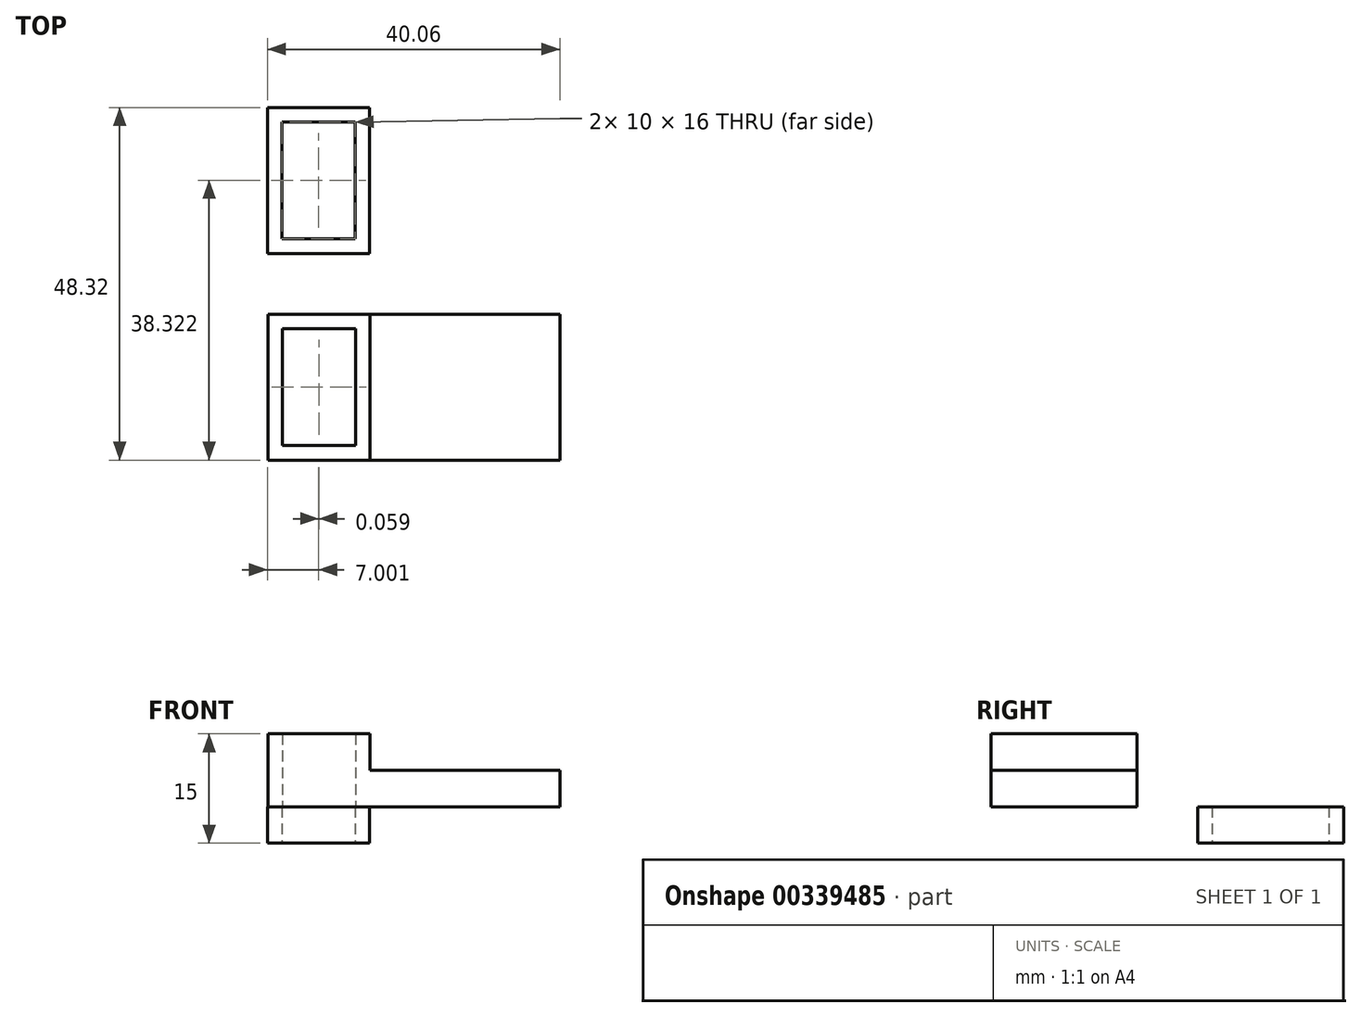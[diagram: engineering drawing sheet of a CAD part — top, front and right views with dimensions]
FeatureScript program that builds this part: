
annotation { "Feature Type Name" : "Feature", "Feature Type Description" : "" }
export const myFeature = defineFeature(function(context is Context, id is Id, definition is map)
    precondition{}
    {
        {
            var Q0;
            Q0=qCreatedBy(makeId("Top.planeOp"),FACE);
            var sketch = newSketch(context, id + "F0", { "sketchPlane" : qUnion([Q0])});
            skLineSegment(sketch, "E0.bottom", {"start": v(0, 20) * mm, "end": v(40, 20) * mm});
            skLineSegment(sketch, "E0.top", {"start": v(0, 0) * mm, "end": v(40, 0) * mm});
            skLineSegment(sketch, "E0.left", {"start": v(0, 20) * mm, "end": v(0, 0) * mm});
            skLineSegment(sketch, "E0.right", {"start": v(40, 20) * mm, "end": v(40, 0) * mm});
            skLineSegment(sketch, "E1.bottom", {"start": v(2, 18) * mm, "end": v(12, 18) * mm});
            skLineSegment(sketch, "E1.top", {"start": v(2, 2) * mm, "end": v(12, 2) * mm});
            skLineSegment(sketch, "E1.left", {"start": v(2, 18) * mm, "end": v(2, 2) * mm});
            skLineSegment(sketch, "E1.right", {"start": v(12, 18) * mm, "end": v(12, 2) * mm});
            skSolve(sketch);
        }
        {
            var Q0;
            Q0=qCreatedBy(makeId("Top.planeOp"),FACE);
            cPlane(context, id + "F1", {"entities" : qUnion([Q0]), "cplaneType" : CPlaneType.OFFSET, "offset" : 5 * mm, "oppositeDirection" : true, "width" : 150 * mm, "height" : 150 * mm});
        }
        {
            var Q0;
            Q0=qCreatedBy(id+"F1.planeOp",FACE);
            var sketch = newSketch(context, id + "F2", { "sketchPlane" : qUnion([Q0])});
            skLineSegment(sketch, "E2.bottom", {"start": v(-0.06, 48.32) * mm, "end": v(13.94, 48.32) * mm});
            skLineSegment(sketch, "E2.top", {"start": v(-0.06, 28.32) * mm, "end": v(13.94, 28.32) * mm});
            skLineSegment(sketch, "E2.left", {"start": v(-0.06, 48.32) * mm, "end": v(-0.06, 28.32) * mm});
            skLineSegment(sketch, "E2.right", {"start": v(13.94, 48.32) * mm, "end": v(13.94, 28.32) * mm});
            skLineSegment(sketch, "E3.bottom", {"start": v(1.94, 46.32) * mm, "end": v(11.94, 46.32) * mm});
            skLineSegment(sketch, "E3.top", {"start": v(1.94, 30.32) * mm, "end": v(11.94, 30.32) * mm});
            skLineSegment(sketch, "E3.left", {"start": v(1.94, 46.32) * mm, "end": v(1.94, 30.32) * mm});
            skLineSegment(sketch, "E3.right", {"start": v(11.94, 46.32) * mm, "end": v(11.94, 30.32) * mm});
            skSolve(sketch);
        }
        {
            var Q0;
            Q0=makeQuery(id+"F2.imprint","IMPRINT",FACE,{"disambiguationData":[TD([[makeQuery(id+"F2.imprint","IMPRINT",EDGE,{"derivedFrom":sQuery(id+"F2.wireOp",EDGE,"E2.bottom")}),-1.0]])]});
            extrude(context, id + "F3", {"entities" : qUnion([Q0]), "depth" : 5 * mm, "offsetDistance" : 25 * mm});
        }
        {
            var Q0;
            Q0=makeQuery(id+"F0.imprint","IMPRINT",FACE,{"disambiguationData":[TD([[makeQuery(id+"F0.imprint","IMPRINT",EDGE,{"derivedFrom":sQuery(id+"F0.wireOp",EDGE,"E0.bottom")}),-1.0]])]});
            extrude(context, id + "F4", {"entities" : qUnion([Q0]), "depth" : 5 * mm, "offsetDistance" : 25 * mm});
        }
        {
            var Q0;
            Q0=makeQuery(id+"F4.opExtrude","CAP_FACE",FACE,{"disambiguationData":[OSD([sQuery(id+"F0.wireOp",EDGE,"E0.bottom"),sQuery(id+"F0.wireOp",EDGE,"E0.top"),sQuery(id+"F0.wireOp",EDGE,"E0.left"),sQuery(id+"F0.wireOp",EDGE,"E0.right"),sQuery(id+"F0.wireOp",EDGE,"E1.bottom"),sQuery(id+"F0.wireOp",EDGE,"E1.top"),sQuery(id+"F0.wireOp",EDGE,"E1.left"),sQuery(id+"F0.wireOp",EDGE,"E1.right")])],"isStart":false});
            var sketch = newSketch(context, id + "F5", { "sketchPlane" : qUnion([Q0])});
            skLineSegment(sketch, "E4.bottom", {"start": v(0, 0) * mm, "end": v(14, 0) * mm});
            skLineSegment(sketch, "E4.top", {"start": v(0, 20) * mm, "end": v(14, 20) * mm});
            skLineSegment(sketch, "E4.left", {"start": v(0, 0) * mm, "end": v(0, 20) * mm});
            skLineSegment(sketch, "E4.right", {"start": v(14, 0) * mm, "end": v(14, 20) * mm});
            skSolve(sketch);
        }
        {
            var Q0;
            Q0=makeQuery(id+"F5.imprint","IMPRINT",FACE,{"disambiguationData":[TD([[makeQuery(id+"F5.imprint","IMPRINT",EDGE,{"derivedFrom":sQuery(id+"F5.wireOp",EDGE,"E4.bottom")}),1.0]])]});
            extrude(context, id + "F6", {"entities" : qUnion([Q0]), "operationType" : NewBodyOperationType.ADD, "depth" : 5 * mm, "offsetDistance" : 25 * mm});
        }
    });
